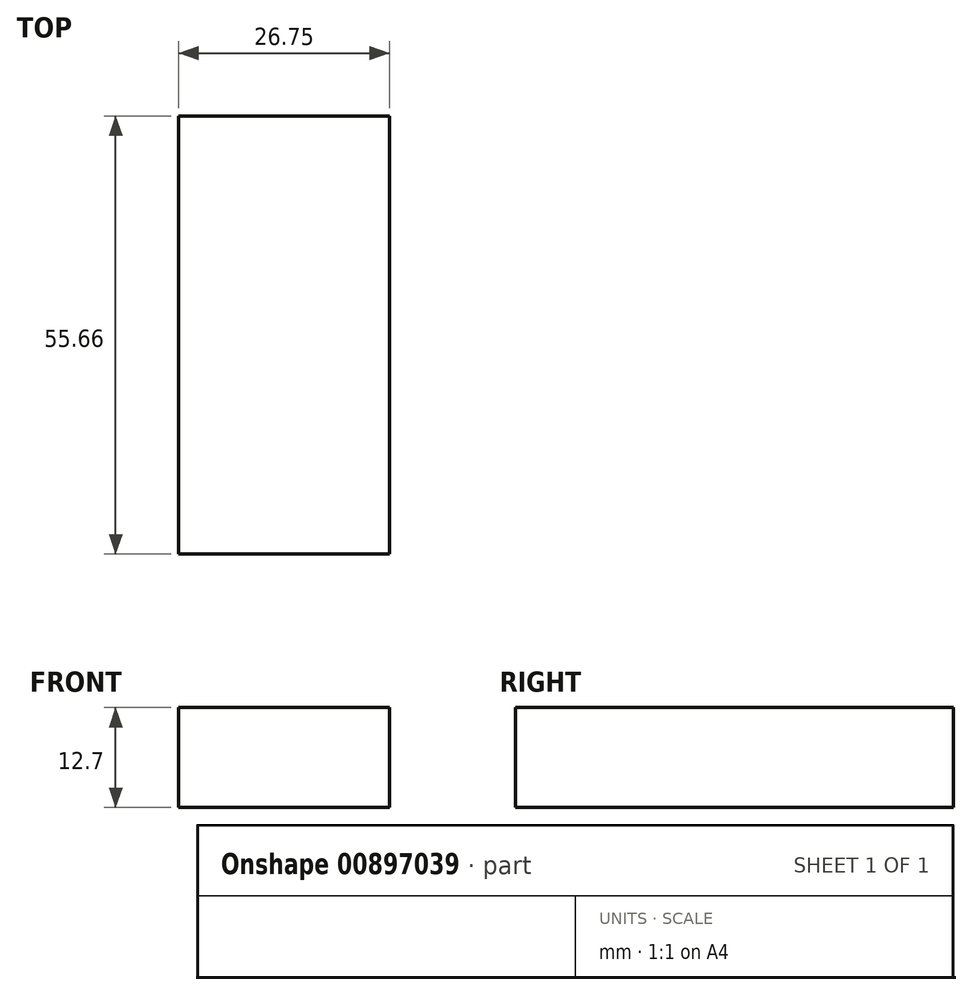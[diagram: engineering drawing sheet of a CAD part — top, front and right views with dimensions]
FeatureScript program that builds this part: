
annotation { "Feature Type Name" : "Feature", "Feature Type Description" : "" }
export const myFeature = defineFeature(function(context is Context, id is Id, definition is map)
    precondition{}
    {
        {
            var Q0;
            Q0=qCreatedBy(makeId("Top.planeOp"),FACE);
            var sketch = newSketch(context, id + "F0", { "sketchPlane" : qUnion([Q0])});
            skLineSegment(sketch, "E0.bottom", {"start": v(0, 0) * mm, "end": v(-26.75, 0) * mm});
            skLineSegment(sketch, "E0.top", {"start": v(0, -55.66) * mm, "end": v(-26.75, -55.66) * mm});
            skLineSegment(sketch, "E0.left", {"start": v(0, 0) * mm, "end": v(0, -55.66) * mm});
            skLineSegment(sketch, "E0.right", {"start": v(-26.75, 0) * mm, "end": v(-26.75, -55.66) * mm});
            skSolve(sketch);
        }
        {
            var Q0;
            Q0=makeQuery(id+"F0.imprint","IMPRINT",FACE,{"disambiguationData":[TD([[makeQuery(id+"F0.imprint","IMPRINT",EDGE,{"derivedFrom":sQuery(id+"F0.wireOp",EDGE,"E0.bottom")}),1.0]])]});
            extrude(context, id + "F1", {"entities" : qUnion([Q0]), "depth" : 12.7 * mm, "offsetDistance" : 25.4 * mm});
        }
    });
